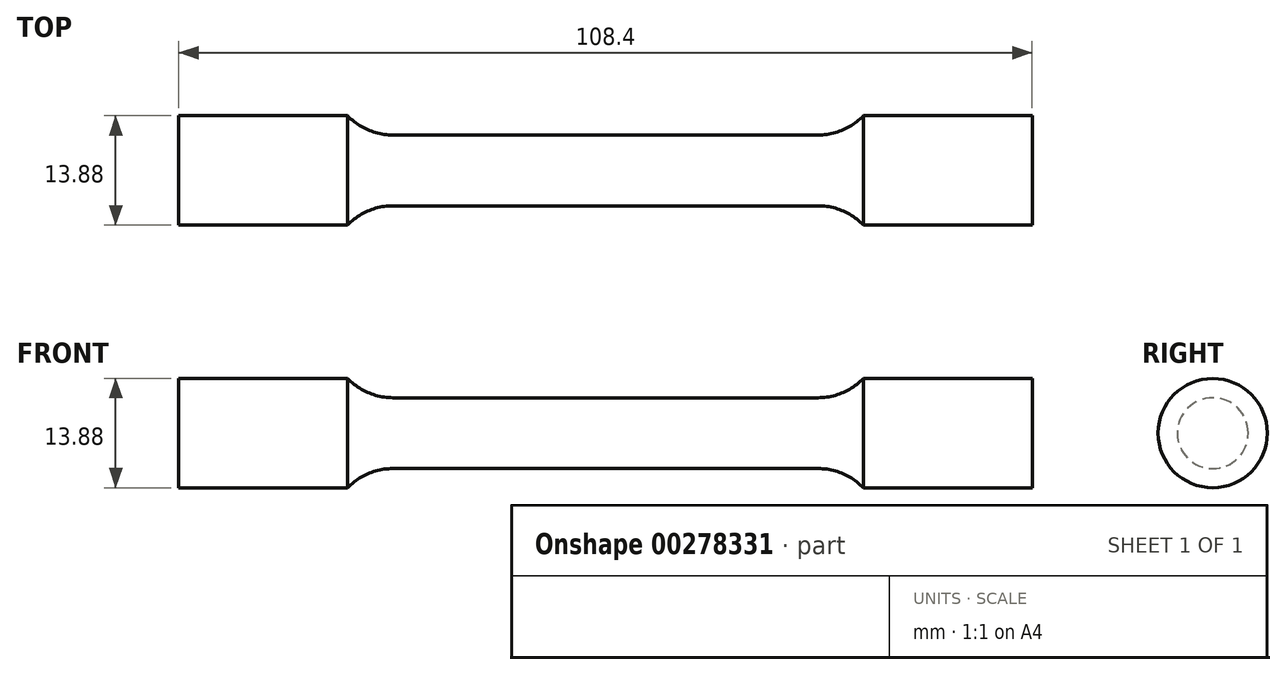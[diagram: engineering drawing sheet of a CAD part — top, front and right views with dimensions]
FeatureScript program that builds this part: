
annotation { "Feature Type Name" : "Feature", "Feature Type Description" : "" }
export const myFeature = defineFeature(function(context is Context, id is Id, definition is map)
    precondition{}
    {
        {
            var Q0;
            Q0=qCreatedBy(makeId("Front.planeOp"),FACE);
            var sketch = newSketch(context, id + "F0", { "sketchPlane" : qUnion([Q0])});
            skLineSegment(sketch, "E0", {"start": v(0, 4.5) * mm, "end": v(27, 4.5) * mm});
            skArc(sketch, "E1", {"start": v(27, 4.5) * mm, "mid": v(30.12, 5.14) * mm, "end": v(32.75, 6.94) * mm});
            skLineSegment(sketch, "E2", {"start": v(32.75, 6.94) * mm, "end": v(54.2, 6.94) * mm});
            skLineSegment(sketch, "E3", {"start": v(54.2, 6.94) * mm, "end": v(54.2, 0) * mm});
            skLineSegment(sketch, "E4.MirrorCS", {"start": v(0, 4.5) * mm, "end": v(-27, 4.5) * mm});
            skLineSegment(sketch, "E5.MirrorCS", {"start": v(-54.2, 6.94) * mm, "end": v(-54.2, 0) * mm});
            skLineSegment(sketch, "E6.MirrorCS", {"start": v(-32.75, 6.94) * mm, "end": v(-54.2, 6.94) * mm});
            skArc(sketch, "E7.MirrorCS", {"start": v(-27, 4.5) * mm, "mid": v(-30.12, 5.14) * mm, "end": v(-32.75, 6.94) * mm});
            skLineSegment(sketch, "E8", {"start": v(-54.2, 0) * mm, "end": v(54.2, 0) * mm});
            skSolve(sketch);
        }
        {
            var Q0;
            Q0 = qSketchRegion(id + "F0", true);
            var Q1;
            Q1=sQuery(id+"F0.wireOp",EDGE,"E8");
            revolve(context, id + "F1", {"entities" : qUnion([Q0]), "axis" : qUnion([Q1]), "revolveType" : RevolveType.FULL});
        }
    });
